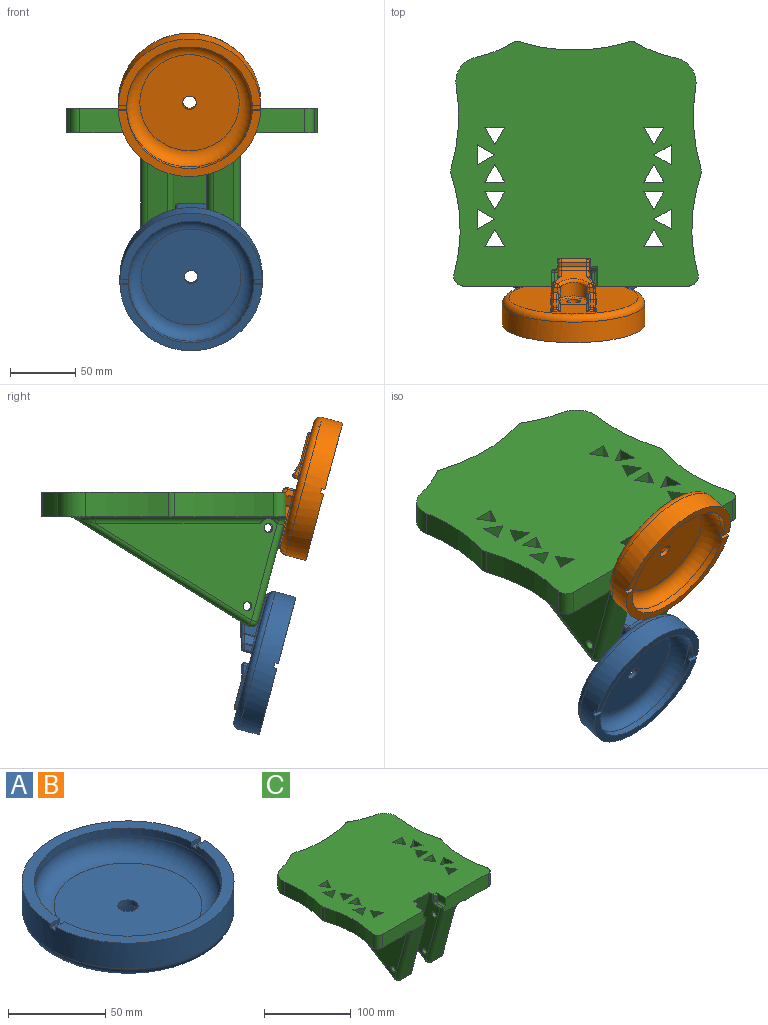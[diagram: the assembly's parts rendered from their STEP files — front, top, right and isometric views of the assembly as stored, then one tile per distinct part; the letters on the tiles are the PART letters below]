
ASSEMBLY  parts=3 mates=2
PART A: 185 faces, bbox 118.3x118.3x46.6 mm
  f0: plane 109.15x52.71mm, normal (0,0,1), area 1001.9mm2, adj f1,f2,f180,f184
  f1: cylinder r=54.61mm len=109.22mm, axis (0,0,-1), area 5558.5mm2, adj f0,f51,f178,f179,f180,f181,f182,f183
  f2: cylinder r=48.26mm len=96.52mm, axis (0,0,1), area 1444mm2, adj f0,f11,f178,f179,f180,f181,f182,f183
  f3: cylinder r=5.21mm len=10.41mm, axis (0,0,-1), area 103.9mm2, adj f10,f49
  f4: cylinder r=4.19mm len=8.38mm, axis (1,0,0), area 46.5mm2, adj f28,f29,f30,f75,f76,f77,f78,f114
  f5: plane 6.26x4.36mm, normal (1,0,0), area 24.5mm2, adj f37,f96,f97,f108,f122
  f6: plane 27.94x19.17mm, normal (0,-0.28,-0.96), area 312.7mm2, adj f35,f36,f37,f38,f39,f40,f41,f43
  f7: plane 9.2x2.71mm, normal (0,-0.28,-0.96), area 24.4mm2, adj f52,f54,f55,f71
  f8: plane 6.26x4.36mm, normal (-1,0,0), area 24.5mm2, adj f40,f99,f100,f111,f115
  f9: cylinder r=11.43mm len=20.98mm, axis (0,0,1), area 249.3mm2, adj f36,f78,f79,f92,f93,f162
  f10: plane 76.2x76.2mm, normal (0,0,1), area 4475.2mm2, adj f3,f11
  f11: torus R=38.1mm, axis (0,0,1), area 4469.1mm2, adj f2,f10
  f12: plane 99.06x97.23mm, normal (0,0,-1), area 5236.7mm2, adj f30,f31,f51,f114,f115,f116,f117,f119
  f13: plane 23.01x2.54mm, normal (0,0,-1), area 58.4mm2, adj f54,f56,f58,f59
  f14: cylinder r=3.49mm len=24.38mm, axis (1,0,0), area 535.1mm2, adj f21,f23
  f15: plane 19.3x18.71mm, normal (0,0,-1), area 361.1mm2, adj f148,f149,f153,f154
  f16: plane 19.3x3.18mm, normal (0,-1,0), area 61.4mm2, adj f42,f46,f48,f148
  f17: plane 9.2x2.71mm, normal (0,-0.28,-0.96), area 24.4mm2, adj f60,f64,f67,f86
  f18: plane 23.01x2.54mm, normal (0,0,-1), area 58.4mm2, adj f61,f63,f64,f65
  f19: plane 10.14x2.84mm, normal (1,0,0), area 14mm2, adj f66,f67,f82,f83,f134
  f20: plane 8.17x7.11mm, normal (0.87,0.5,0), area 58.5mm2, adj f39,f96,f102,f124
  f21: plane 30.18x19.08mm, normal (1,0,0), area 438.8mm2, adj f14,f41,f42,f44,f102,f103,f126,f127
  f22: plane 19.31x18.22mm, normal (0,1,0), area 341.6mm2, adj f136,f150,f154,f156
  f23: plane 30.62x19.08mm, normal (-1,0,0), area 442.6mm2, adj f14,f45,f47,f48,f105,f106,f119,f120
  f24: plane 8.04x6.67mm, normal (-0.87,0.5,0), area 54.4mm2, adj f43,f99,f105,f117
  f25: plane 10.14x2.84mm, normal (-1,0,0), area 14mm2, adj f55,f57,f68,f70,f130
  f26: plane 14.97x6.02mm, normal (1,0,0), area 53mm2, adj f52,f53,f56,f72,f74,f75,f165,f172
  f27: plane 14.97x6.02mm, normal (-1,0,0), area 53mm2, adj f60,f61,f62,f85,f88,f89,f169,f175
  f28: plane 5.36x3.3mm, normal (0,-1,0), area 17.7mm2, adj f4,f38,f79,f80,f111,f112
  f29: plane 2.08x1.02mm, normal (0,1,0), area 2.1mm2, adj f4,f68,f71,f74
  f30: plane 8.11x3.15mm, normal (1,0,0), area 17.2mm2, adj f4,f12,f114,f131
  f31: plane 8.11x3.15mm, normal (-1,0,0), area 17.2mm2, adj f12,f34,f121,f135
  f32: plane 2.08x1.02mm, normal (0,1,0), area 2.1mm2, adj f34,f82,f86,f88
  f33: plane 5.36x3.3mm, normal (0,-1,0), area 17.7mm2, adj f34,f35,f93,f94,f108,f109
  f34: cylinder r=4.19mm len=8.38mm, axis (1,0,0), area 46.5mm2, adj f31,f32,f33,f89,f90,f91,f92,f121
  f35: cylinder r=2.54mm len=3.24mm, axis (-1,0,0), area 8.1mm2, adj f6,f33,f95,f110
  f36: bspline ~24.78x8.09mm, area 93mm2, adj f6,f9,f80,f81,f94,f95
  f37: cylinder r=2.54mm len=5.05mm, axis (0,0.96,-0.28), area 15mm2, adj f5,f6,f98,f109,f110
  f38: cylinder r=2.54mm len=3.24mm, axis (-1,0,0), area 8.1mm2, adj f6,f28,f81,f113
  f39: cylinder r=2.54mm len=9.98mm, axis (-0.48,0.84,-0.25), area 37.8mm2, adj f6,f20,f97,f98,f103,f104
  f40: cylinder r=2.54mm len=5.05mm, axis (0,-0.96,0.28), area 15mm2, adj f6,f8,f101,f112,f113
  f41: cylinder r=2.54mm len=9.44mm, axis (0,0.96,-0.28), area 34.3mm2, adj f6,f21,f44,f104
  f42: cylinder r=2.54mm len=3.18mm, axis (0,0,-1), area 12.7mm2, adj f16,f21,f44,f146
  f43: cylinder r=2.54mm len=9.54mm, axis (-0.48,-0.84,0.25), area 35.5mm2, adj f6,f24,f100,f101,f106,f107
  f44: bspline ~4.87x4.36mm, area 17.8mm2, adj f21,f41,f42,f46
  f45: cylinder r=2.54mm len=9.88mm, axis (0,-0.96,0.28), area 36.1mm2, adj f6,f23,f47,f107
  f46: cylinder r=2.54mm len=19.3mm, axis (-1,0,0), area 63mm2, adj f6,f16,f44,f47
  f47: torus R=5.08mm, axis (1,0,0), area 17.8mm2, adj f23,f45,f46,f48
  f48: cylinder r=2.54mm len=3.18mm, axis (0,0,1), area 12.7mm2, adj f16,f23,f47,f151
  f49: plane 27.94x22.29mm, normal (0,0,-1), area 448.9mm2, adj f3,f159,f160,f161,f162,f163,f164,f165
  f50: plane 20.32x0.64mm, normal (0,1,0), area 12.9mm2, adj f167,f171,f173,f176
  f51: torus R=49.53mm, axis (0,0,-1), area 2541.3mm2, adj f1,f12,f120,f127,f136
  f52: cylinder r=1.27mm len=9.56mm, axis (0,0.96,-0.28), area 19.1mm2, adj f7,f26,f53,f72
  f53: torus R=2.54mm, axis (-1,0,0), area 1mm2, adj f26,f52,f54,f56
  f54: cylinder r=1.27mm len=2.54mm, axis (-1,0,0), area 0.9mm2, adj f7,f13,f53,f57
  f55: cylinder r=1.27mm len=9.56mm, axis (0,-0.96,0.28), area 19.1mm2, adj f7,f25,f57,f70
  f56: cylinder r=1.27mm len=23.01mm, axis (0,1,0), area 45.9mm2, adj f13,f26,f53,f128,f142
  f57: torus R=2.54mm, axis (1,0,0), area 1mm2, adj f25,f54,f55,f59
  f58: cylinder r=1.27mm len=2.54mm, axis (1,0,0), area 5.1mm2, adj f13,f129,f142,f144
  f59: cylinder r=1.27mm len=23.01mm, axis (0,-1,0), area 45.9mm2, adj f13,f57,f130,f144
  f60: cylinder r=1.27mm len=9.56mm, axis (0,-0.96,0.28), area 19.1mm2, adj f17,f27,f62,f85
  f61: cylinder r=1.27mm len=23.01mm, axis (0,-1,0), area 45.9mm2, adj f18,f27,f62,f132,f138
  f62: torus R=2.54mm, axis (-1,0,0), area 1mm2, adj f27,f60,f61,f64
  f63: cylinder r=1.27mm len=2.54mm, axis (1,0,0), area 5.1mm2, adj f18,f133,f138,f140
  f64: cylinder r=1.27mm len=2.54mm, axis (-1,0,0), area 0.9mm2, adj f17,f18,f62,f66
  f65: cylinder r=1.27mm len=23.01mm, axis (0,1,0), area 45.9mm2, adj f18,f66,f134,f140
  f66: torus R=2.54mm, axis (1,0,0), area 1mm2, adj f19,f64,f65,f67
  f67: cylinder r=1.27mm len=9.56mm, axis (0,0.96,-0.28), area 19.1mm2, adj f17,f19,f66,f83
  f68: cylinder r=2.03mm len=2.84mm, axis (0,0,-1), area 7.9mm2, adj f25,f29,f69,f131
  f69: bspline ~2.14x2.03mm, area 2.8mm2, adj f68,f70,f71
  f70: torus R=0.76mm, axis (1,0,0), area 0.9mm2, adj f25,f55,f69,f71
  f71: cylinder r=2.03mm len=2.61mm, axis (1,0,0), area 7.2mm2, adj f7,f29,f69,f70,f72,f73
  f72: torus R=0.76mm, axis (-1,0,0), area 0.9mm2, adj f26,f52,f71,f73
  f73: bspline ~2.14x2.03mm, area 2.8mm2, adj f71,f72,f74
  f74: cylinder r=2.03mm len=2.84mm, axis (0,0,1), area 7.9mm2, adj f26,f29,f73,f75
  f75: torus R=6.22mm, axis (-1,0,0), area 11.6mm2, adj f4,f26,f74,f76,f163
  f76: bspline ~5.02x2.31mm, area 4.7mm2, adj f4,f75,f77,f161
  f77: bspline ~4.24x2.13mm, area 3.9mm2, adj f4,f76,f78,f159
  f78: bspline ~5.99x2.81mm, area 8.9mm2, adj f4,f9,f77,f79,f160
  f79: cylinder r=2.03mm len=5.28mm, axis (0,0,1), area 11.7mm2, adj f9,f28,f78,f80
  f80: bspline ~1.83x1.22mm, area 0.5mm2, adj f28,f36,f79,f81
  f81: bspline ~2.92x2.12mm, area 2.7mm2, adj f36,f38,f80
  f82: cylinder r=2.03mm len=2.84mm, axis (0,0,1), area 7.9mm2, adj f19,f32,f84,f135
  f83: torus R=0.76mm, axis (1,0,0), area 0.9mm2, adj f19,f67,f84,f86
  f84: bspline ~2.46x2.03mm, area 2.8mm2, adj f82,f83,f86
  f85: torus R=0.76mm, axis (-1,0,0), area 0.9mm2, adj f27,f60,f86,f87
  f86: cylinder r=2.03mm len=2.61mm, axis (1,0,0), area 7.2mm2, adj f17,f32,f83,f84,f85,f87
  f87: bspline ~2.14x2.03mm, area 2.8mm2, adj f85,f86,f88
  f88: cylinder r=2.03mm len=2.84mm, axis (0,0,-1), area 7.9mm2, adj f27,f32,f87,f89
  f89: torus R=6.22mm, axis (-1,0,0), area 11.6mm2, adj f27,f34,f88,f90,f170
  f90: bspline ~5.02x2.31mm, area 4.7mm2, adj f34,f89,f91,f168
  f91: bspline ~4.24x2.13mm, area 3.9mm2, adj f34,f90,f92,f166
  f92: bspline ~6.6x3.39mm, area 8.9mm2, adj f9,f34,f91,f93,f164
  f93: cylinder r=2.03mm len=5.28mm, axis (0,0,1), area 11.7mm2, adj f9,f33,f92,f94
  f94: bspline ~1.85x1.41mm, area 0.5mm2, adj f33,f36,f93,f95
  f95: bspline ~2.92x2.12mm, area 2.7mm2, adj f35,f36,f94
  f96: cylinder r=1.27mm len=6.08mm, axis (0,0,1), area 4mm2, adj f5,f20,f97,f123
  f97: bspline ~0.78x0.68mm, area 0.2mm2, adj f5,f39,f96,f98
  f98: bspline ~2.54x2.44mm, area 1mm2, adj f37,f39,f97
  f99: cylinder r=1.27mm len=6.08mm, axis (0,0,1), area 4mm2, adj f8,f24,f100,f116
  f100: bspline ~0.66x0.35mm, area 0.2mm2, adj f8,f43,f99,f101
  f101: bspline ~2.68x2.54mm, area 1mm2, adj f40,f43,f100
  f102: cylinder r=1.27mm len=8.17mm, axis (0,0,-1), area 5.4mm2, adj f20,f21,f103,f125
  f103: bspline ~1.2x0.77mm, area 0.3mm2, adj f21,f39,f102,f104
  f104: bspline ~2.7x2.43mm, area 1mm2, adj f39,f41,f103
  f105: cylinder r=1.27mm len=8.04mm, axis (0,0,-1), area 5.3mm2, adj f23,f24,f106,f118
  f106: bspline ~1.8x0.89mm, area 0.3mm2, adj f23,f43,f105,f107
  f107: bspline ~2.7x2.67mm, area 1mm2, adj f43,f45,f106
  f108: cylinder r=1.27mm len=4.99mm, axis (0,0,-1), area 9.9mm2, adj f5,f33,f109,f121
  f109: bspline ~1.32x1.27mm, area 1.2mm2, adj f33,f37,f108,f110
  f110: bspline ~2.75x2.51mm, area 2.5mm2, adj f35,f37,f109
  f111: cylinder r=1.27mm len=4.99mm, axis (0,0,1), area 9.9mm2, adj f8,f28,f112,f114
  f112: bspline ~1.51x1.41mm, area 1.2mm2, adj f28,f40,f111,f113
  f113: bspline ~2.75x2.51mm, area 2.5mm2, adj f38,f40,f112
  f114: torus R=2.54mm, axis (0,0,-1), area 3.7mm2, adj f4,f12,f30,f111,f115
  f115: cylinder r=1.27mm len=4.36mm, axis (0,1,0), area 8.7mm2, adj f8,f12,f114,f116
  f116: torus R=2.54mm, axis (0,0,-1), area 1.8mm2, adj f12,f99,f115,f117
  f117: cylinder r=1.27mm len=7.3mm, axis (0.5,0.87,0), area 15.4mm2, adj f12,f24,f116,f118
  f118: sphere r=1.27mm, area 0.8mm2, adj f105,f117,f119
  f119: cylinder r=1.27mm len=29.87mm, axis (0,1,0), area 59.6mm2, adj f12,f23,f118,f120
  f120: bspline ~7.21x3.8mm, area 4.3mm2, adj f23,f51,f119,f158
  f121: torus R=2.54mm, axis (0,0,-1), area 3.7mm2, adj f12,f31,f34,f108,f122
  f122: cylinder r=1.27mm len=4.36mm, axis (0,-1,0), area 8.7mm2, adj f5,f12,f121,f123
  f123: torus R=2.54mm, axis (0,0,-1), area 1.8mm2, adj f12,f96,f122,f124
  f124: cylinder r=1.27mm len=7.75mm, axis (0.5,-0.87,0), area 16.4mm2, adj f12,f20,f123,f125
  f125: sphere r=1.27mm, area 0.8mm2, adj f102,f124,f126
  f126: cylinder r=1.27mm len=29.5mm, axis (0,-1,0), area 58.9mm2, adj f12,f21,f125,f127
  f127: bspline ~7.15x3.73mm, area 4.2mm2, adj f21,f51,f126,f145
  f128: cylinder r=1.27mm len=21.59mm, axis (0,-1,0), area 40.5mm2, adj f12,f56,f141,f172
  f129: cylinder r=1.27mm len=7.62mm, axis (-1,0,0), area 10.1mm2, adj f12,f58,f141,f143
  f130: cylinder r=1.27mm len=35.69mm, axis (0,1,0), area 68.7mm2, adj f12,f25,f59,f131,f143
  f131: torus R=3.3mm, axis (0,0,-1), area 5.6mm2, adj f4,f12,f30,f68,f130
  f132: cylinder r=1.27mm len=21.59mm, axis (0,1,0), area 40.5mm2, adj f12,f61,f137,f175
  f133: cylinder r=1.27mm len=7.62mm, axis (-1,0,0), area 10.1mm2, adj f12,f63,f137,f139
  f134: cylinder r=1.27mm len=35.69mm, axis (0,-1,0), area 68.7mm2, adj f12,f19,f65,f135,f139
  f135: torus R=3.3mm, axis (0,0,-1), area 5.6mm2, adj f12,f31,f34,f82,f134
  f136: bspline ~30.22x5.07mm, area 93.8mm2, adj f22,f51,f145,f147,f157,f158
  f137: bspline ~2.54x2.54mm, area 1.7mm2, adj f132,f133,f138
  f138: sphere r=1.27mm, area 2.5mm2, adj f61,f63,f137
  f139: bspline ~2.54x2.54mm, area 1.7mm2, adj f133,f134,f140
  f140: sphere r=1.27mm, area 2.5mm2, adj f63,f65,f139
  f141: bspline ~2.54x2.54mm, area 1.7mm2, adj f128,f129,f142
  f142: sphere r=1.27mm, area 2.5mm2, adj f56,f58,f141
  f143: bspline ~2.54x2.54mm, area 1.7mm2, adj f129,f130,f144
  f144: sphere r=1.27mm, area 2.5mm2, adj f58,f59,f143
  f145: bspline ~4.05x3.74mm, area 5.5mm2, adj f127,f136,f147
  f146: sphere r=2.54mm, area 10.1mm2, adj f42,f148,f149
  f147: bspline ~2.76x2.68mm, area 2.8mm2, adj f21,f136,f145,f150
  f148: cylinder r=2.54mm len=19.3mm, axis (-1,0,0), area 77mm2, adj f15,f16,f146,f151
  f149: cylinder r=2.54mm len=18.71mm, axis (0,1,0), area 74.6mm2, adj f15,f21,f146,f152
  f150: cylinder r=2.54mm len=18.18mm, axis (0,0,-1), area 72.5mm2, adj f21,f22,f147,f152
  f151: sphere r=2.54mm, area 10.1mm2, adj f48,f148,f153
  f152: sphere r=2.54mm, area 6.5mm2, adj f149,f150,f154
  f153: cylinder r=2.54mm len=18.71mm, axis (0,-1,0), area 74.6mm2, adj f15,f23,f151,f155
  f154: cylinder r=2.54mm len=19.3mm, axis (-1,0,0), area 77mm2, adj f15,f22,f152,f155
  f155: sphere r=2.54mm, area 6.5mm2, adj f153,f154,f156
  f156: cylinder r=2.54mm len=18.22mm, axis (0,0,1), area 72.7mm2, adj f22,f23,f155,f157
  f157: bspline ~4.36x2.83mm, area 2.7mm2, adj f23,f136,f156,f158
  f158: bspline ~4.08x3.72mm, area 5.4mm2, adj f120,f136,f157
  f159: bspline ~3.89x1.22mm, area 2.2mm2, adj f49,f77,f160,f161
  f160: bspline ~3.29x2.59mm, area 3.2mm2, adj f49,f78,f159,f162
  f161: bspline ~4.18x1.09mm, area 2.7mm2, adj f49,f76,f159,f163
  f162: torus R=10.16mm, axis (0,0,-1), area 50.8mm2, adj f9,f49,f160,f164
  f163: bspline ~3.44x1.63mm, area 3.5mm2, adj f49,f75,f161,f165
  f164: bspline ~3.29x2.59mm, area 3.2mm2, adj f49,f92,f162,f166
  f165: cylinder r=1.27mm len=12.43mm, axis (0,-1,0), area 24.8mm2, adj f26,f49,f163,f174
  f166: bspline ~3.82x1.2mm, area 2.2mm2, adj f49,f91,f164,f168
  f167: cylinder r=1.27mm len=20.32mm, axis (-1,0,0), area 40.5mm2, adj f49,f50,f174,f177
  f168: bspline ~3.93x1.09mm, area 2.7mm2, adj f49,f90,f166,f170
  f169: cylinder r=1.27mm len=12.43mm, axis (0,1,0), area 24.8mm2, adj f27,f49,f170,f177
  f170: bspline ~3.44x1.63mm, area 3.5mm2, adj f49,f89,f168,f169
  f171: cylinder r=1.27mm len=20.32mm, axis (1,0,0), area 40.5mm2, adj f12,f50,f172,f175
  f172: torus R=2.54mm, axis (-1,0,0), area 5.4mm2, adj f26,f128,f171,f173
  f173: cylinder r=1.27mm len=1.27mm, axis (0,0,1), area 1.3mm2, adj f26,f50,f172,f174
  f174: sphere r=1.27mm, area 2.5mm2, adj f165,f167,f173
  f175: torus R=2.54mm, axis (-1,0,0), area 5.4mm2, adj f27,f132,f171,f176
  f176: cylinder r=1.27mm len=1.27mm, axis (0,0,-1), area 1.3mm2, adj f27,f50,f175,f177
  f177: sphere r=1.27mm, area 2.5mm2, adj f167,f169,f176
  f178: plane 109.15x52.71mm, normal (0,0,1), area 1001.9mm2, adj f1,f2,f181,f183
  f179: plane 6.39x3.81mm, normal (0,0,1), area 24.2mm2, adj f1,f2,f180,f181
  f180: plane 6.35x2.54mm, normal (0,1,0), area 16.1mm2, adj f0,f1,f2,f179
  f181: plane 6.35x2.54mm, normal (0,-1,0), area 16.1mm2, adj f1,f2,f178,f179
  f182: plane 6.39x3.81mm, normal (0,0,1), area 24.2mm2, adj f1,f2,f183,f184
  f183: plane 6.35x2.54mm, normal (0,-1,0), area 16.1mm2, adj f1,f2,f178,f182
  f184: plane 6.35x2.54mm, normal (0,1,0), area 16.1mm2, adj f0,f1,f2,f182
PART B: same geometry as A
PART C: 202 faces, bbox 196.6x193.7x107.7 mm
  f0: plane 193.62x188.89mm, normal (0,0,-1), area 17241.8mm2, adj f2,f3,f4,f8,f9,f10,f12,f17
  f1: plane 4.05x1.1mm, normal (1,0,0), area 2.2mm2, adj f8,f85,f86,f118
  f2: cylinder r=5.08mm len=8.64mm, axis (0,1,0), area 47.3mm2, adj f0,f3,f18,f97,f104
  f3: bspline ~5.59x5.58mm, area 6.9mm2, adj f0,f2,f4,f97
  f4: cylinder r=5.08mm len=131.69mm, axis (0,1,0), area 1040.3mm2, adj f0,f3,f18,f97,f201
  f5: cylinder r=3.43mm len=15.88mm, axis (1,0,0), area 342mm2, adj f13,f96
  f6: cylinder r=3.43mm len=15.88mm, axis (1,0,0), area 342mm2, adj f13,f83
  f7: plane 137.48x74.12mm, normal (1,0,0), area 4957.4mm2, adj f10,f84,f87,f88,f89,f90,f91,f92
  f8: cylinder r=5.08mm len=8.64mm, axis (0,-1,0), area 54mm2, adj f0,f1,f9,f85,f116
  f9: bspline ~5.59x5.58mm, area 8.3mm2, adj f0,f8,f10,f84,f85
  f10: cylinder r=5.08mm len=131.69mm, axis (0,-1,0), area 1043.8mm2, adj f0,f7,f9,f84,f199
  f11: plane 192.22x187.49mm, normal (0,0,1), area 30998mm2, adj f12,f13,f14,f17,f19,f20,f21,f22
  f12: plane 77.86x23.43mm, normal (0,-1,0), area 1330.7mm2, adj f0,f11,f15,f34,f35,f37,f100,f114
  f13: plane 98.25x40.81mm, normal (-1,0,0), area 1696.4mm2, adj f5,f6,f11,f31,f37,f38,f40,f112
  f14: plane 98.25x40.81mm, normal (1,0,0), area 1696.4mm2, adj f11,f29,f30,f31,f43,f45,f46,f109
  f15: plane 80.52x21.57mm, normal (0,-0.97,-0.26), area 1275.1mm2, adj f12,f114,f116,f117,f118
  f16: plane 133.44x82.75mm, normal (0,0.53,-0.85), area 9426mm2, adj f105,f108,f111,f112,f113,f117,f120,f200
  f17: plane 75.32x23.43mm, normal (0,-1,0), area 1282.3mm2, adj f0,f11,f28,f32,f44,f46,f99,f104
  f18: plane 139.38x77.79mm, normal (-1,0,0), area 5123.7mm2, adj f2,f4,f29,f30,f97,f105,f106
  f19: cylinder r=101.6mm len=29.52mm, axis (0,0,-1), area 607.1mm2, adj f0,f11,f26,f103
  f20: cylinder r=139.7mm len=63.37mm, axis (0,0,-1), area 1220.3mm2, adj f0,f11,f26,f98
  f21: cylinder r=127mm len=75.64mm, axis (0,0,-1), area 1463.8mm2, adj f0,f11,f98,f99
  f22: cylinder r=127mm len=75.64mm, axis (0,0,-1), area 1463.8mm2, adj f0,f11,f100,f101
  f23: cylinder r=139.7mm len=62.94mm, axis (0,0,-1), area 1211.9mm2, adj f0,f11,f27,f101
  f24: cylinder r=101.6mm len=31.58mm, axis (0,0,-1), area 647.1mm2, adj f0,f11,f27,f102
  f25: cylinder r=139.7mm len=84.55mm, axis (0,0,-1), area 1636.4mm2, adj f0,f11,f102,f103
  f26: cylinder r=19.05mm len=21.76mm, axis (0,0,-1), area 550.9mm2, adj f0,f11,f19,f20
  f27: cylinder r=19.05mm len=21.78mm, axis (0,0,-1), area 557.5mm2, adj f0,f11,f23,f24
  f28: plane 80.52x21.57mm, normal (0,-0.97,-0.26), area 1275.1mm2, adj f17,f104,f106,f108,f109
  f29: cylinder r=3.43mm len=25.4mm, axis (1,0,0), area 547.2mm2, adj f14,f18
  f30: cylinder r=3.43mm len=25.4mm, axis (1,0,0), area 547.2mm2, adj f14,f18
  f31: plane 85.58x25.4mm, normal (0,-0.97,-0.26), area 2250.4mm2, adj f11,f13,f14,f112
  f32: plane 10.16x8.89mm, normal (1,0,0), area 90.3mm2, adj f11,f17,f41,f44
  f33: plane 6.35x2.54mm, normal (0,-1,0), area 16.1mm2, adj f34,f36,f39,f40
  f34: plane 15.24x8.89mm, normal (-1,0,0), area 114.3mm2, adj f11,f12,f33,f35,f39
  f35: cylinder r=2.54mm len=12.7mm, axis (0,1,0), area 45.6mm2, adj f12,f34,f36,f37
  f36: cylinder r=2.54mm len=2.54mm, axis (-1,0,0), area 5.1mm2, adj f33,f35,f38
  f37: cylinder r=2.54mm len=10.16mm, axis (0,1,0), area 35.6mm2, adj f12,f13,f35,f38,f114
  f38: torus R=5.08mm, axis (-1,0,0), area 21.7mm2, adj f13,f36,f37,f40
  f39: cylinder r=2.54mm len=5.08mm, axis (1,0,0), area 15.2mm2, adj f11,f33,f34,f40
  f40: cylinder r=2.54mm len=8.89mm, axis (0,0,1), area 30.4mm2, adj f13,f33,f38,f39
  f41: cylinder r=2.54mm len=8.89mm, axis (0,0,-1), area 35.5mm2, adj f11,f32,f42,f43
  f42: sphere r=2.54mm, area 10.1mm2, adj f41,f44,f45
  f43: cylinder r=2.54mm len=8.89mm, axis (0,0,-1), area 35.5mm2, adj f11,f14,f41,f45
  f44: cylinder r=2.54mm len=10.16mm, axis (0,-1,0), area 40.5mm2, adj f17,f32,f42,f46
  f45: torus R=5.08mm, axis (-1,0,0), area 21.7mm2, adj f14,f42,f43,f46
  f46: cylinder r=2.54mm len=10.16mm, axis (0,-1,0), area 35.6mm2, adj f14,f17,f44,f45,f109
  f47: plane 19.05x15.24mm, normal (0,1,0), area 290.3mm2, adj f0,f11,f48,f49
  f48: plane 19.05x13.2mm, normal (-0.87,-0.5,0), area 290.3mm2, adj f0,f11,f47,f49
  f49: plane 19.05x13.2mm, normal (0.87,-0.5,0), area 290.3mm2, adj f0,f11,f47,f48
  f50: plane 19.05x15.24mm, normal (0,-1,0), area 290.3mm2, adj f0,f11,f51,f52
  f51: plane 19.05x13.2mm, normal (0.87,0.5,0), area 290.3mm2, adj f0,f11,f50,f52
  f52: plane 19.05x13.2mm, normal (-0.87,0.5,0), area 290.3mm2, adj f0,f11,f50,f51
  f53: plane 19.05x13.2mm, normal (-0.5,-0.87,0), area 290.3mm2, adj f0,f11,f54,f55
  f54: plane 19.05x15.24mm, normal (1,0,0), area 290.3mm2, adj f0,f11,f53,f55
  f55: plane 19.05x13.2mm, normal (-0.5,0.87,0), area 290.3mm2, adj f0,f11,f53,f54
  f56: plane 19.05x13.2mm, normal (-0.5,-0.87,0), area 290.3mm2, adj f0,f11,f57,f58
  f57: plane 19.05x15.24mm, normal (1,0,0), area 290.3mm2, adj f0,f11,f56,f58
  f58: plane 19.05x13.2mm, normal (-0.5,0.87,0), area 290.3mm2, adj f0,f11,f56,f57
  f59: plane 19.05x13.2mm, normal (-0.87,0.5,0), area 290.3mm2, adj f0,f11,f60,f61
  f60: plane 19.05x15.24mm, normal (0,-1,0), area 290.3mm2, adj f0,f11,f59,f61
  f61: plane 19.05x13.2mm, normal (0.87,0.5,0), area 290.3mm2, adj f0,f11,f59,f60
  f62: plane 19.05x15.24mm, normal (-1,0,0), area 290.3mm2, adj f0,f11,f63,f64
  f63: plane 19.05x13.2mm, normal (0.5,-0.87,0), area 290.3mm2, adj f0,f11,f62,f64
  f64: plane 19.05x13.2mm, normal (0.5,0.87,0), area 290.3mm2, adj f0,f11,f62,f63
  f65: plane 19.05x13.2mm, normal (0.87,0.5,0), area 290.3mm2, adj f0,f11,f66,f67
  f66: plane 19.05x13.2mm, normal (-0.87,0.5,0), area 290.3mm2, adj f0,f11,f65,f67
  f67: plane 19.05x15.24mm, normal (0,-1,0), area 290.3mm2, adj f0,f11,f65,f66
  f68: plane 19.05x13.2mm, normal (0.5,0.87,0), area 290.3mm2, adj f0,f11,f69,f70
  f69: plane 19.05x15.24mm, normal (-1,0,0), area 290.3mm2, adj f0,f11,f68,f70
  f70: plane 19.05x13.2mm, normal (0.5,-0.87,0), area 290.3mm2, adj f0,f11,f68,f69
  f71: plane 19.05x13.2mm, normal (0.87,-0.5,0), area 290.3mm2, adj f0,f11,f72,f73
  f72: plane 19.05x15.24mm, normal (0,1,0), area 290.3mm2, adj f0,f11,f71,f73
  f73: plane 19.05x13.2mm, normal (-0.87,-0.5,0), area 290.3mm2, adj f0,f11,f71,f72
  f74: plane 19.05x13.2mm, normal (0.87,-0.5,0), area 290.3mm2, adj f0,f11,f75,f76
  f75: plane 19.05x15.24mm, normal (0,1,0), area 290.3mm2, adj f0,f11,f74,f76
  f76: plane 19.05x13.2mm, normal (-0.87,-0.5,0), area 290.3mm2, adj f0,f11,f74,f75
  f77: plane 19.05x13.2mm, normal (0.87,0.5,0), area 290.3mm2, adj f0,f11,f78,f79
  f78: plane 19.05x13.2mm, normal (-0.87,0.5,0), area 290.3mm2, adj f0,f11,f77,f79
  f79: plane 19.05x15.24mm, normal (0,-1,0), area 290.3mm2, adj f0,f11,f77,f78
  f80: plane 19.05x15.24mm, normal (0,1,0), area 290.3mm2, adj f0,f11,f81,f82
  f81: plane 19.05x13.2mm, normal (-0.87,-0.5,0), area 290.3mm2, adj f0,f11,f80,f82
  f82: plane 19.05x13.2mm, normal (0.87,-0.5,0), area 290.3mm2, adj f0,f11,f80,f81
  f83: plane 13.21x11.44mm, normal (1,0,0), area 76.4mm2, adj f6,f84,f85,f86,f87,f88,f89
  f84: plane 10.95x5.93mm, normal (0,-0.5,-0.87), area 65.4mm2, adj f7,f9,f10,f83,f85,f89
  f85: plane 10.95x5.93mm, normal (0,0.5,-0.87), area 65.4mm2, adj f1,f8,f9,f83,f84,f86
  f86: plane 9.53x6.61mm, normal (0,1,0), area 62.9mm2, adj f1,f83,f85,f87,f118
  f87: plane 9.53x5.72mm, normal (0,0.5,0.87), area 62.9mm2, adj f7,f83,f86,f88,f118
  f88: plane 9.53x5.72mm, normal (0,-0.5,0.87), area 62.9mm2, adj f7,f83,f87,f89
  f89: plane 9.53x6.6mm, normal (0,-1,0), area 62.9mm2, adj f7,f83,f84,f88
  f90: plane 9.53x6.61mm, normal (0,1,0), area 62.9mm2, adj f7,f91,f95,f96,f118
  f91: plane 9.53x5.72mm, normal (0,0.5,0.87), area 62.9mm2, adj f7,f90,f92,f96,f118
  f92: plane 9.53x5.72mm, normal (0,-0.5,0.87), area 62.9mm2, adj f7,f91,f93,f96
  f93: plane 9.53x6.6mm, normal (0,-1,0), area 62.9mm2, adj f7,f92,f94,f96
  f94: plane 9.53x5.72mm, normal (0,-0.5,-0.87), area 62.9mm2, adj f7,f93,f95,f96
  f95: plane 9.53x5.72mm, normal (0,0.5,-0.87), area 62.9mm2, adj f7,f90,f94,f96
  f96: plane 13.21x11.44mm, normal (1,0,0), area 76.4mm2, adj f5,f90,f91,f92,f93,f94,f95
  f97: cylinder r=6.99mm len=12.3mm, axis (1,0,0), area 12.7mm2, adj f2,f3,f4,f18
  f98: cylinder r=7.62mm len=19.05mm, axis (0,0,-1), area 90.7mm2, adj f0,f11,f20,f21
  f99: cylinder r=7.62mm len=19.05mm, axis (0,0,-1), area 267.5mm2, adj f0,f11,f17,f21
  f100: cylinder r=7.62mm len=19.05mm, axis (0,0,-1), area 267.5mm2, adj f0,f11,f12,f22
  f101: cylinder r=7.62mm len=19.05mm, axis (0,0,-1), area 90.7mm2, adj f0,f11,f22,f23
  f102: cylinder r=5.08mm len=19.05mm, axis (0,0,-1), area 81.3mm2, adj f0,f11,f24,f25
  f103: cylinder r=5.08mm len=19.05mm, axis (0,0,-1), area 81.3mm2, adj f0,f11,f19,f25
  f104: bspline ~18.06x10.16mm, area 106.4mm2, adj f0,f2,f17,f28,f106
  f105: cylinder r=5.08mm len=136.12mm, axis (0,0.85,0.53), area 1187.6mm2, adj f16,f18,f107,f201
  f106: cylinder r=5.08mm len=75.44mm, axis (0,-0.26,0.97), area 612.3mm2, adj f18,f28,f104,f107
  f107: sphere r=5.08mm, area 51.6mm2, adj f105,f106,f108
  f108: cylinder r=5.08mm len=15.24mm, axis (-1,0,0), area 144.3mm2, adj f16,f28,f107,f110
  f109: cylinder r=5.08mm len=88.55mm, axis (0,-0.26,0.97), area 699.7mm2, adj f14,f17,f28,f46,f110
  f110: sphere r=5.08mm, area 46.1mm2, adj f108,f109,f111
  f111: cylinder r=5.08mm len=25.23mm, axis (0,-0.85,-0.53), area 191.5mm2, adj f14,f16,f110,f112
  f112: cylinder r=5.08mm len=35.56mm, axis (-1,0,0), area 270mm2, adj f13,f14,f16,f31,f111,f113
  f113: cylinder r=5.08mm len=25.23mm, axis (0,0.85,0.53), area 191.5mm2, adj f13,f16,f112,f115
  f114: cylinder r=5.08mm len=88.55mm, axis (0,0.26,-0.97), area 699.7mm2, adj f12,f13,f15,f37,f115
  f115: sphere r=5.08mm, area 51.6mm2, adj f113,f114,f117
  f116: bspline ~18.06x10.16mm, area 106.4mm2, adj f0,f8,f12,f15,f118
  f117: cylinder r=5.08mm len=15.24mm, axis (-1,0,0), area 144.3mm2, adj f15,f16,f115,f119
  f118: cylinder r=5.08mm len=75.44mm, axis (0,0.26,-0.97), area 610.2mm2, adj f1,f7,f15,f86,f87,f90,f91,f116
  f119: sphere r=5.08mm, area 46.1mm2, adj f117,f118,f120
  f120: cylinder r=5.08mm len=136.12mm, axis (0,-0.85,-0.53), area 1187.6mm2, adj f7,f16,f119,f199
  f121: plane 9.71x1.88mm, normal (-0.98,-0.19,0), area 10mm2, adj f0,f122,f132,f133
  f122: plane 7.91x1.02mm, normal (0,1,0), area 8mm2, adj f0,f121,f123,f133
  f123: plane 1.57x1.02mm, normal (0.98,0.19,0), area 1.6mm2, adj f0,f122,f124,f133
  f124: plane 5.88x1.02mm, normal (0,-1,0), area 6mm2, adj f0,f123,f125,f133
  f125: plane 2.56x1.02mm, normal (0.98,0.19,0), area 2.6mm2, adj f0,f124,f126,f133
  f126: plane 5.18x1.02mm, normal (0,1,0), area 5.3mm2, adj f0,f125,f127,f133
  f127: plane 1.57x1.02mm, normal (0.98,0.19,0), area 1.6mm2, adj f0,f126,f128,f133
  f128: plane 5.18x1.02mm, normal (0,-1,0), area 5.3mm2, adj f0,f127,f129,f133
  f129: plane 2.44x1.02mm, normal (0.98,0.19,0), area 2.5mm2, adj f0,f128,f130,f133
  f130: plane 5.6x1.02mm, normal (0,1,0), area 5.7mm2, adj f0,f129,f131,f133
  f131: plane 1.57x1.02mm, normal (0.98,0.19,0), area 1.6mm2, adj f0,f130,f132,f133
  f132: plane 7.63x1.02mm, normal (0,-1,0), area 7.8mm2, adj f0,f121,f131,f133
  f133: plane 9.71x9.51mm, normal (0,0,-1), area 45.9mm2, adj f121,f122,f123,f124,f125,f126,f127,f128
  f134: extruded ~1.46x1.02mm, area 1.6mm2, adj f135,f146,f147,f197
  f135: extruded ~1.09x1.02mm, area 1.1mm2, adj f134,f136,f147,f197
  f136: plane 3.11x1.02mm, normal (-0.99,0.15,0), area 3.2mm2, adj f135,f137,f147,f197
  f137: plane 2.72x1.02mm, normal (0,-1,0), area 2.8mm2, adj f136,f146,f147,f197
  f138: plane 2.48x1.02mm, normal (-0.99,0.15,0), area 2.5mm2, adj f0,f139,f145,f147
  f139: plane 2.01x1.02mm, normal (0,1,0), area 2mm2, adj f0,f138,f140,f147
  f140: plane 9.71x1.64mm, normal (0.99,-0.17,0), area 10mm2, adj f0,f139,f141,f147
  f141: plane 2.4x1.02mm, normal (0,-1,0), area 2.4mm2, adj f0,f140,f142,f147
  f142: plane 9.71x5.42mm, normal (-0.87,-0.49,0), area 11.3mm2, adj f0,f141,f143,f147
  f143: plane 2.03x1.02mm, normal (0,1,0), area 2.1mm2, adj f0,f142,f144,f147
  f144: plane 2.48x1.34mm, normal (0.88,0.48,0), area 2.9mm2, adj f0,f143,f145,f147
  f145: plane 3.7x1.02mm, normal (0,1,0), area 3.8mm2, adj f0,f138,f144,f147
  f146: plane 2.74x1.46mm, normal (0.88,0.47,0), area 3.2mm2, adj f134,f137,f147,f197
  f147: plane 9.71x9.46mm, normal (0,0,-1), area 40.8mm2, adj f134,f135,f136,f137,f138,f139,f140,f141
  f148: plane 1.99x1.02mm, normal (0,-1,0), area 2mm2, adj f149,f163,f164,f198
  f149: plane 3.15x1.02mm, normal (0.98,0.19,0), area 3.3mm2, adj f148,f150,f164,f198
  f150: plane 1.81x1.02mm, normal (0,1,0), area 1.8mm2, adj f149,f151,f164,f198
  f151: extruded ~1.27x1.02mm, area 1.4mm2, adj f150,f152,f164,f198
  f152: extruded ~1.07x1.02mm, area 1.2mm2, adj f151,f153,f164,f198
  f153: extruded ~1.31x1.02mm, area 1.5mm2, adj f152,f163,f164,f198
  f154: extruded ~2.64x1.02mm, area 2.8mm2, adj f0,f155,f162,f164
  f155: plane 3.73x1.02mm, normal (0,-1,0), area 3.8mm2, adj f0,f154,f156,f164
  f156: plane 9.71x1.88mm, normal (-0.98,-0.19,0), area 10mm2, adj f0,f155,f157,f164
  f157: plane 2.02x1.02mm, normal (0,1,0), area 2.1mm2, adj f0,f156,f158,f164
  f158: plane 3.42x1.02mm, normal (0.98,0.19,0), area 3.5mm2, adj f0,f157,f159,f164
  f159: plane 2.6x1.02mm, normal (0,1,0), area 2.6mm2, adj f0,f158,f160,f164
  f160: extruded ~2.83x1.02mm, area 3.1mm2, adj f0,f159,f161,f164
  f161: extruded ~2.47x1.06mm, area 2.8mm2, adj f0,f160,f162,f164
  f162: extruded ~2.14x1.02mm, area 2.5mm2, adj f0,f154,f161,f164
  f163: extruded ~1.6x1.02mm, area 1.7mm2, adj f148,f153,f164,f198
  f164: plane 9.71x9.18mm, normal (0,0,-1), area 41.3mm2, adj f148,f149,f150,f151,f152,f153,f154,f155
  f165: plane 4.41x2.45mm, normal (-0.87,0.48,0), area 5.1mm2, adj f0,f166,f176,f177
  f166: plane 2.25x1.02mm, normal (0,1,0), area 2.3mm2, adj f0,f165,f167,f177
  f167: plane 5.46x3.2mm, normal (0.86,-0.51,0), area 6.4mm2, adj f0,f166,f168,f177
  f168: plane 5.15x4.24mm, normal (0.64,0.77,0), area 6.8mm2, adj f0,f167,f169,f177
  f169: plane 2.54x1.02mm, normal (0,-1,0), area 2.6mm2, adj f0,f168,f170,f177
  f170: plane 5.24x4.4mm, normal (-0.64,-0.77,0), area 7mm2, adj f0,f169,f171,f177
  f171: plane 4.4x1.02mm, normal (0.98,0.2,0), area 4.6mm2, adj f0,f170,f172,f177
  f172: plane 2.03x1.02mm, normal (0,-1,0), area 2.1mm2, adj f0,f171,f173,f177
  f173: plane 9.71x1.88mm, normal (-0.98,-0.19,0), area 10mm2, adj f0,f172,f174,f177
  f174: plane 2.01x1.02mm, normal (0,1,0), area 2mm2, adj f0,f173,f175,f177
  f175: plane 3.56x1.02mm, normal (0.98,0.19,0), area 3.7mm2, adj f0,f174,f176,f177
  f176: plane 1.45x1.02mm, normal (0.5,0.86,0), area 1.7mm2, adj f0,f165,f175,f177
  f177: plane 10.8x9.71mm, normal (0,0,-1), area 43.4mm2, adj f165,f166,f167,f168,f169,f170,f171,f172
  f178: extruded ~1.84x1.02mm, area 2mm2, adj f0,f179,f195,f196
  f179: extruded ~3.15x1.02mm, area 3.4mm2, adj f0,f178,f180,f196
  f180: extruded ~2.62x1.16mm, area 3mm2, adj f0,f179,f181,f196
  f181: extruded ~1.38x1.02mm, area 1.5mm2, adj f0,f180,f182,f196
  f182: extruded ~1.16x1.02mm, area 1.4mm2, adj f0,f181,f183,f196
  f183: plane 1.89x1.02mm, normal (0.25,0.97,0), area 2mm2, adj f0,f182,f184,f196
  f184: extruded ~2.02x1.37mm, area 2.5mm2, adj f0,f183,f185,f196
  f185: extruded ~2.6x1.02mm, area 2.8mm2, adj f0,f184,f186,f196
  f186: extruded ~2.95x1.02mm, area 3.1mm2, adj f0,f185,f187,f196
  f187: extruded ~2.1x2.02mm, area 3mm2, adj f0,f186,f188,f196
  f188: extruded ~3.1x1.02mm, area 3.3mm2, adj f0,f187,f189,f196
  f189: extruded ~2.15x1.02mm, area 2.3mm2, adj f0,f188,f190,f196
  f190: extruded ~1.45x1.42mm, area 2.1mm2, adj f0,f189,f191,f196
  f191: extruded ~2.27x1.02mm, area 2.4mm2, adj f0,f190,f192,f196
  f192: extruded ~4.58x2.56mm, area 5.6mm2, adj f0,f191,f193,f196
  f193: plane 1.56x1.02mm, normal (0.46,-0.89,0), area 1.8mm2, adj f0,f192,f194,f196
  f194: extruded ~2.88x1.78mm, area 3.6mm2, adj f0,f193,f195,f196
  f195: extruded ~1.68x1.02mm, area 1.9mm2, adj f0,f178,f194,f196
  f196: plane 9.99x9.67mm, normal (0,0,-1), area 39mm2, adj f178,f179,f180,f181,f182,f183,f184,f185
  f197: plane 4.2x2.72mm, normal (0,0,-1), area 5.5mm2, adj f134,f135,f136,f137,f146
  f198: plane 4.13x3.15mm, normal (0,0,-1), area 11mm2, adj f148,f149,f150,f151,f152,f153,f163
  f199: bspline ~19.28x10.16mm, area 109.9mm2, adj f0,f10,f120,f200
  f200: cylinder r=5.08mm len=66.04mm, axis (-1,0,0), area 186.2mm2, adj f0,f16,f199,f201
  f201: bspline ~20.12x10.16mm, area 109.9mm2, adj f0,f4,f105,f200
PLACE A rot(axis=(1,0,0),105deg) t=(-20.85,-99.86,-107.35)mm
PLACE B rot(axis=(0,0.79,-0.61),180deg) t=(-22.12,-135.64,26.2)mm
PLACE C t=(-21.49,-34.4,2.73)mm
MATE pin_slot B.f14 <-> C.f6  axis (-1,0,0) through (-34.19,-107.38,-5.66)mm
MATE pin_slot A.f14 <-> C.f5  axis (1,0,0) through (-8.79,-91.31,-65.63)mm
